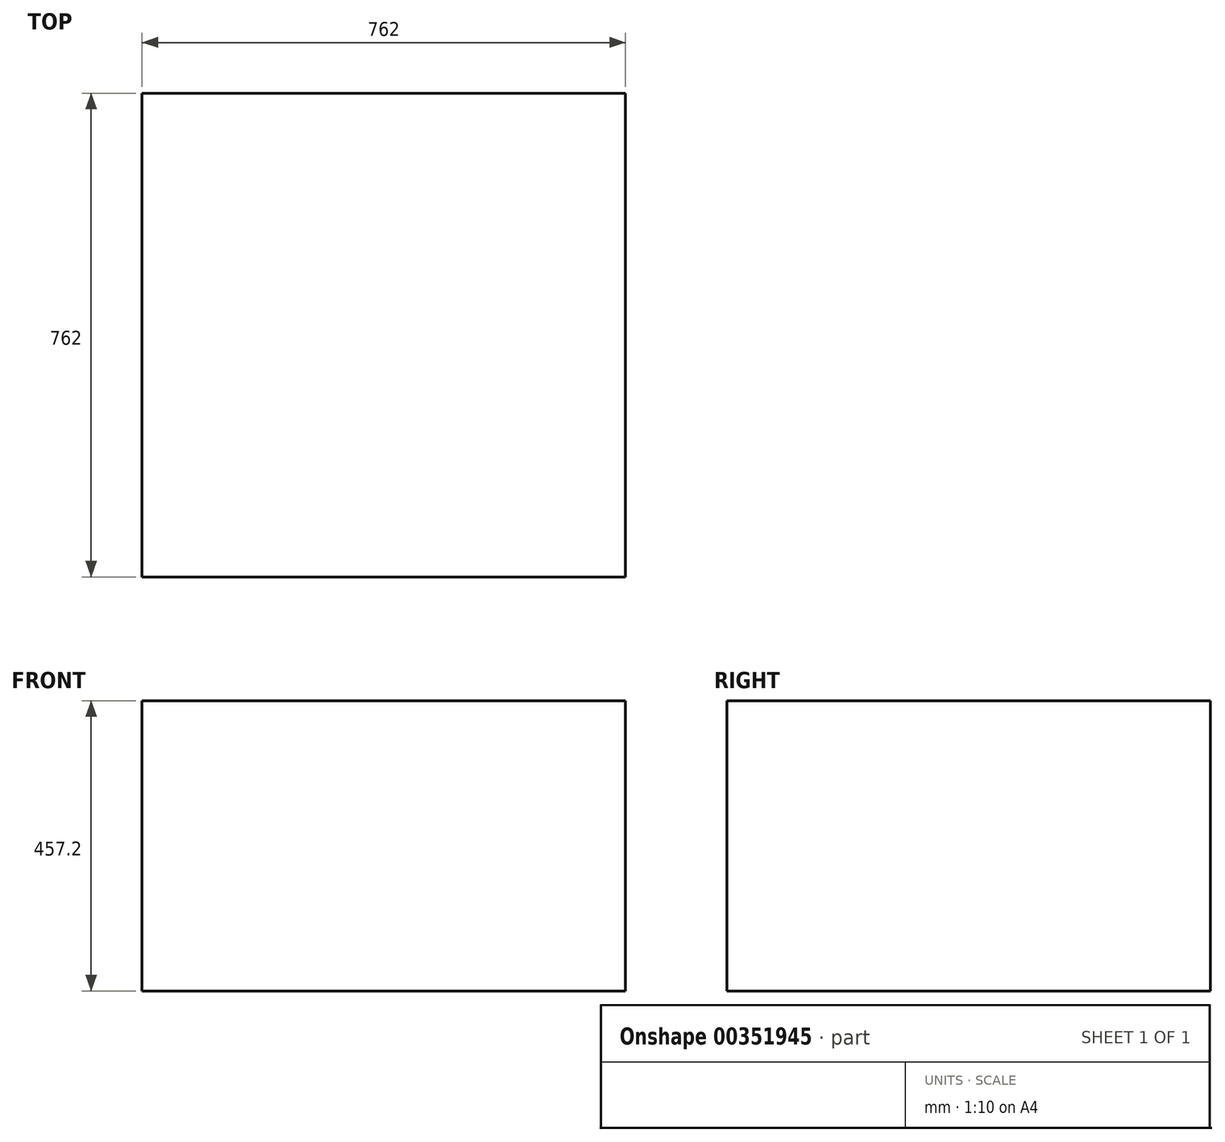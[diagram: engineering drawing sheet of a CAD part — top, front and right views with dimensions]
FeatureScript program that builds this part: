
annotation { "Feature Type Name" : "Feature", "Feature Type Description" : "" }
export const myFeature = defineFeature(function(context is Context, id is Id, definition is map)
    precondition{}
    {
        {
            var Q0;
            Q0=qCreatedBy(makeId("Front.planeOp"),FACE);
            var sketch = newSketch(context, id + "F0", { "sketchPlane" : qUnion([Q0])});
            skLineSegment(sketch, "E0.bottom", {"start": v(0, 0) * mm, "end": v(762, 0) * mm});
            skLineSegment(sketch, "E0.top", {"start": v(0, 457.2) * mm, "end": v(762, 457.2) * mm});
            skLineSegment(sketch, "E0.left", {"start": v(0, 0) * mm, "end": v(0, 457.2) * mm});
            skLineSegment(sketch, "E0.right", {"start": v(762, 0) * mm, "end": v(762, 457.2) * mm});
            skSolve(sketch);
        }
        {
            var Q0;
            Q0 = qSketchRegion(id + "F0", true);
            extrude(context, id + "F1", {"entities" : qUnion([Q0]), "oppositeDirection" : true, "depth" : 762 * mm});
        }
    });
